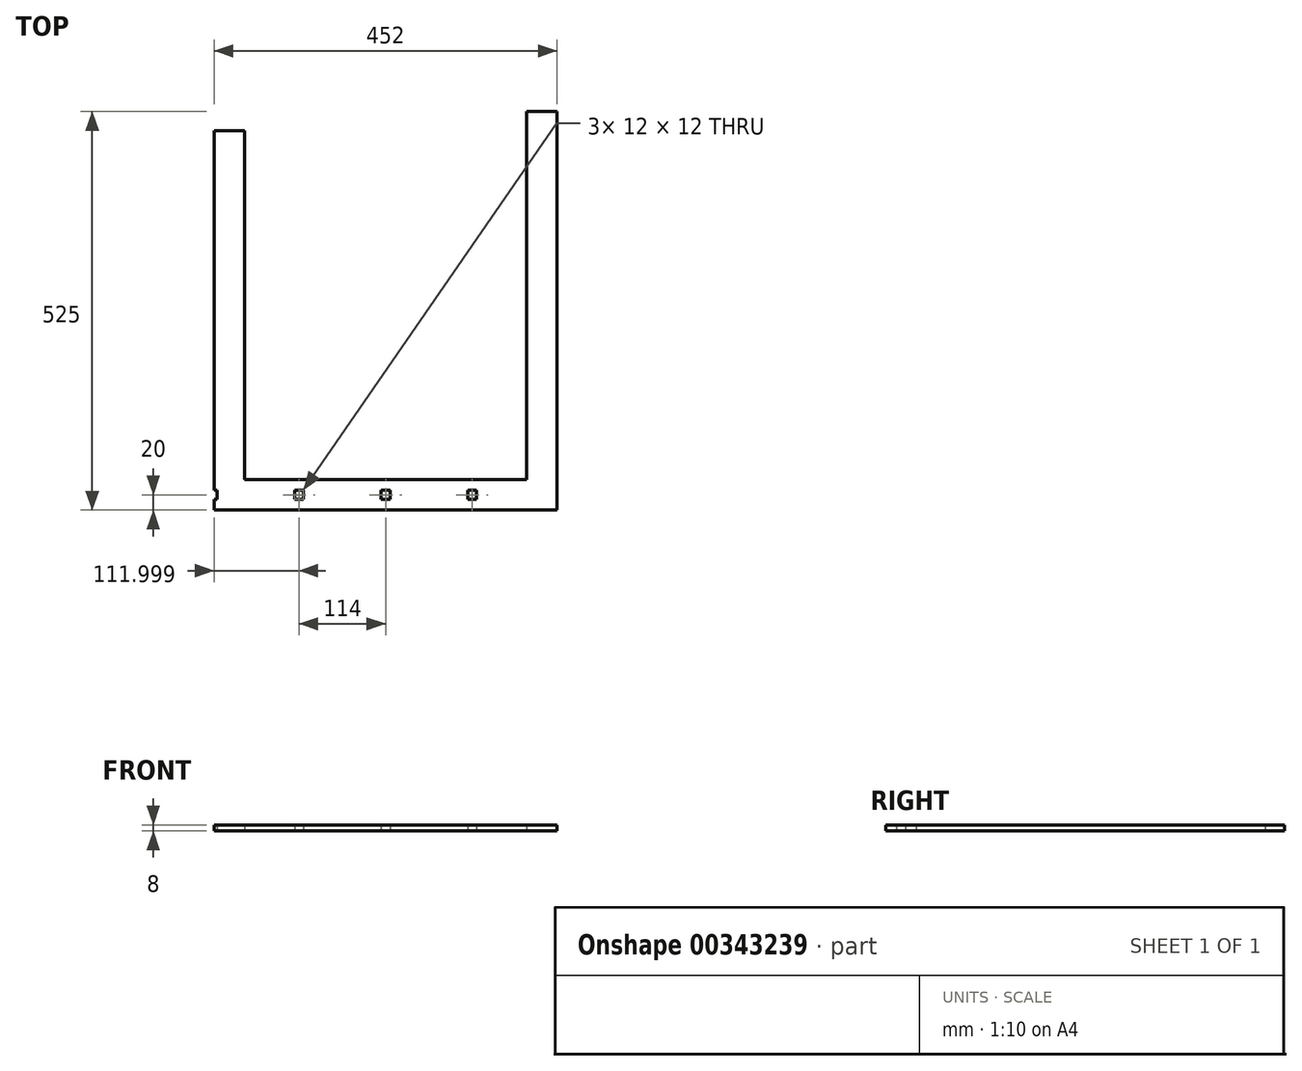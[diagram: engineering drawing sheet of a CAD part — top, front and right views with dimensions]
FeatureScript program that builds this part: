
annotation { "Feature Type Name" : "Feature", "Feature Type Description" : "" }
export const myFeature = defineFeature(function(context is Context, id is Id, definition is map)
    precondition{}
    {
        {
            var Q0;
            Q0=qCreatedBy(makeId("Top.planeOp"),FACE);
            var sketch = newSketch(context, id + "F0", { "sketchPlane" : qUnion([Q0])});
            skLineSegment(sketch, "E0", {"start": v(-227.25, 322.64) * mm, "end": v(-187.25, 322.64) * mm});
            skLineSegment(sketch, "E1", {"start": v(-187.25, 322.64) * mm, "end": v(-187.25, -137.36) * mm});
            skLineSegment(sketch, "E2", {"start": v(-187.25, -137.36) * mm, "end": v(184.75, -137.36) * mm});
            skLineSegment(sketch, "E3", {"start": v(184.75, -137.36) * mm, "end": v(184.75, 367.64) * mm});
            skLineSegment(sketch, "E4", {"start": v(184.75, 367.64) * mm, "end": v(224.75, 367.64) * mm});
            skLineSegment(sketch, "E5", {"start": v(224.75, 367.64) * mm, "end": v(224.75, -177.36) * mm});
            skLineSegment(sketch, "E6", {"start": v(224.75, -177.36) * mm, "end": v(-227.25, -177.36) * mm});
            skLineSegment(sketch, "E7", {"start": v(-227.25, -177.36) * mm, "end": v(-227.25, 322.64) * mm});
            skLineSegment(sketch, "E8", {"start": v(-1.25, -177.36) * mm, "end": v(-1.25, -137.36) * mm, "construction": true});
            skLineSegment(sketch, "E9", {"start": v(-1.25, -137.36) * mm, "end": v(-1.25, -157.36) * mm});
            skLineSegment(sketch, "E10", {"start": v(-1.25, -157.36) * mm, "end": v(224.75, -157.36) * mm, "construction": true});
            skLineSegment(sketch, "E11", {"start": v(184.75, -137.36) * mm, "end": v(224.75, -177.36) * mm, "construction": true});
            skLineSegment(sketch, "E12", {"start": v(204.75, -157.36) * mm, "end": v(204.75, 367.64) * mm, "construction": true});
            skLineSegment(sketch, "E13.bottom", {"start": v(4.75, -151.36) * mm, "end": v(-7.25, -151.36) * mm});
            skLineSegment(sketch, "E13.top", {"start": v(4.75, -163.36) * mm, "end": v(-7.25, -163.36) * mm});
            skLineSegment(sketch, "E13.left", {"start": v(4.75, -151.36) * mm, "end": v(4.75, -163.36) * mm});
            skLineSegment(sketch, "E13.right", {"start": v(-7.25, -151.36) * mm, "end": v(-7.25, -163.36) * mm});
            skPoint(sketch, "E13.middle", {"position": v(-1.25, -157.36) * mm});
            skLineSegment(sketch, "E14.1.0.0", {"start": v(118.75, -163.36) * mm, "end": v(106.75, -163.36) * mm});
            skLineSegment(sketch, "E14.1.0.1", {"start": v(106.75, -151.36) * mm, "end": v(106.75, -163.36) * mm});
            skLineSegment(sketch, "E14.1.0.2", {"start": v(118.75, -151.36) * mm, "end": v(118.75, -163.36) * mm});
            skPoint(sketch, "E14.1.0.3", {"position": v(112.75, -157.36) * mm});
            skLineSegment(sketch, "E14.1.0.4", {"start": v(118.75, -151.36) * mm, "end": v(106.75, -151.36) * mm});
            skLineSegment(sketch, "E14.direction1", {"start": v(-7.25, -163.36) * mm, "end": v(106.75, -163.36) * mm, "construction": true});
            skLineSegment(sketch, "E15.1.0.0", {"start": v(-121.25, -151.36) * mm, "end": v(-121.25, -163.36) * mm});
            skLineSegment(sketch, "E15.1.0.1", {"start": v(-109.25, -151.36) * mm, "end": v(-121.25, -151.36) * mm});
            skLineSegment(sketch, "E15.1.0.2", {"start": v(-109.25, -151.36) * mm, "end": v(-109.25, -163.36) * mm});
            skLineSegment(sketch, "E15.1.0.3", {"start": v(-109.25, -163.36) * mm, "end": v(-121.25, -163.36) * mm});
            skPoint(sketch, "E15.1.0.4", {"position": v(-115.25, -157.36) * mm});
            skLineSegment(sketch, "E15.2.0.0", {"start": v(-235.25, -151.36) * mm, "end": v(-235.25, -163.36) * mm});
            skLineSegment(sketch, "E15.2.0.1", {"start": v(-223.25, -151.36) * mm, "end": v(-235.25, -151.36) * mm});
            skLineSegment(sketch, "E15.2.0.2", {"start": v(-223.25, -151.36) * mm, "end": v(-223.25, -163.36) * mm});
            skLineSegment(sketch, "E15.2.0.3", {"start": v(-223.25, -163.36) * mm, "end": v(-235.25, -163.36) * mm});
            skPoint(sketch, "E15.2.0.4", {"position": v(-229.25, -157.36) * mm});
            skLineSegment(sketch, "E15.direction1", {"start": v(-7.25, -163.36) * mm, "end": v(-121.25, -163.36) * mm, "construction": true});
            skPoint(sketch, "E16.MirrorP", {"position": v(204.75, -157.36) * mm});
            skLineSegment(sketch, "E17.direction2", {"start": v(226.75, -157.36) * mm, "end": v(226.75, -43.36) * mm, "construction": true});
            skPoint(sketch, "E18.0.0.5", {"position": v(226.75, 412.64) * mm});
            skLineSegment(sketch, "E19.0", {"start": v(184.75, 347.64) * mm, "end": v(224.75, 347.64) * mm});
            skSolve(sketch);
        }
        {
            var Q0;
            Q0=makeQuery(id+"F0.imprint","IMPRINT",FACE,{"disambiguationData":[TD([[makeQuery(id+"F0.imprint","IMPRINT",EDGE,{"derivedFrom":sQuery(id+"F0.wireOp",EDGE,"E0")}),-1.0]])]});
            extrude(context, id + "F1", {"entities" : qUnion([Q0]), "depth" : 8 * mm});
        }
    });
